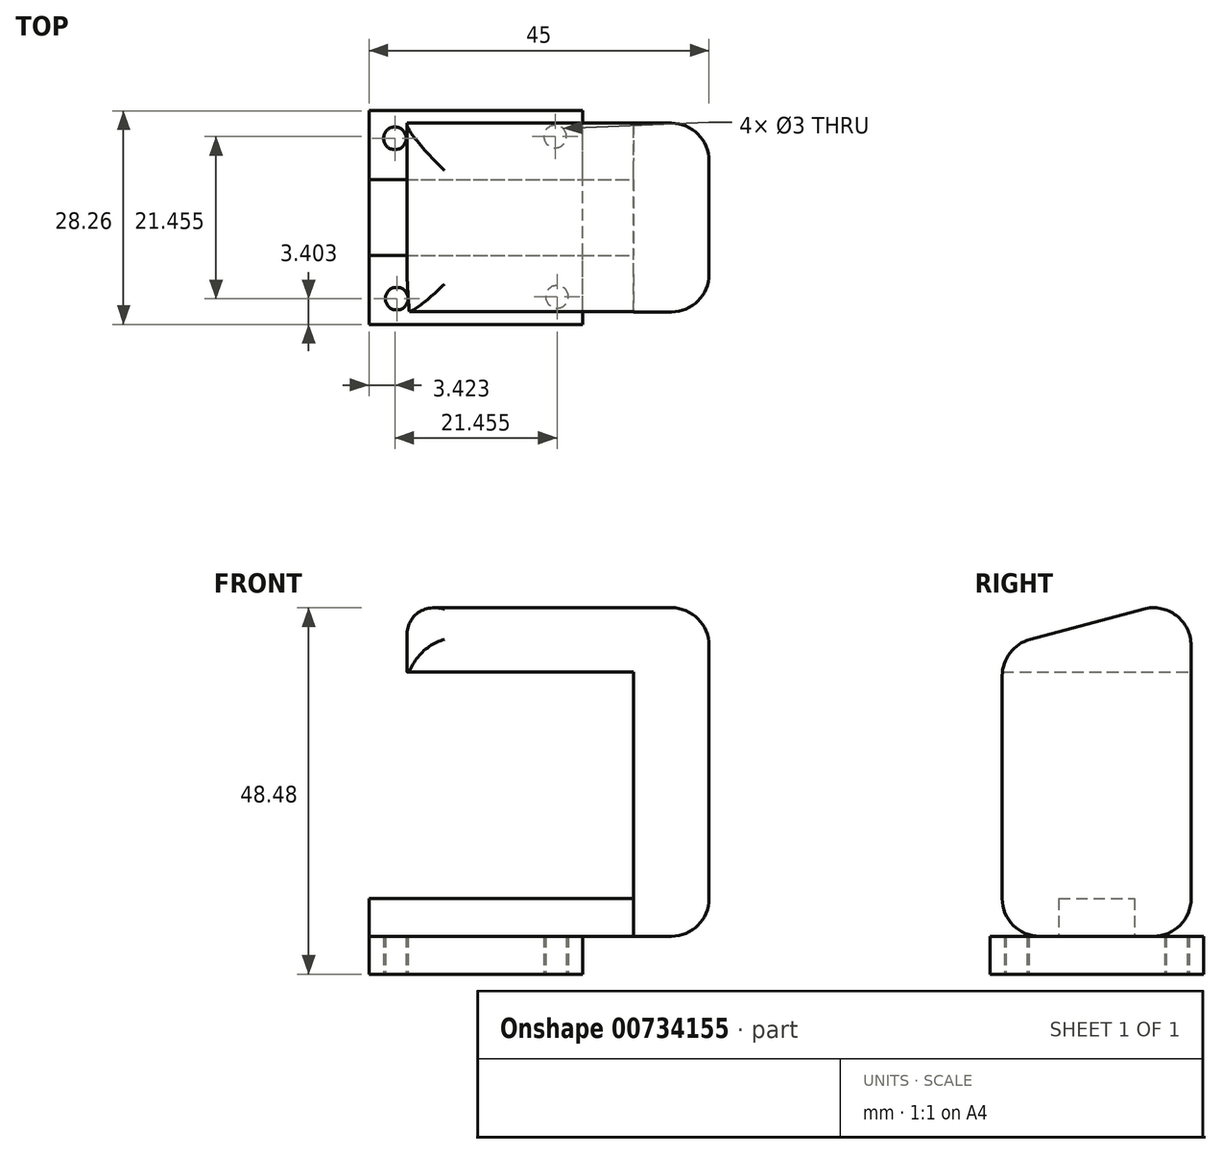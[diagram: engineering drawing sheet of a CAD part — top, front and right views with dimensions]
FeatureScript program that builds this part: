
annotation { "Feature Type Name" : "Feature", "Feature Type Description" : "" }
export const myFeature = defineFeature(function(context is Context, id is Id, definition is map)
    precondition{}
    {
        {
            var Q0;
            Q0=qCreatedBy(makeId("Top.planeOp"),FACE);
            var sketch = newSketch(context, id + "F0", { "sketchPlane" : qUnion([Q0])});
            skLineSegment(sketch, "E0.bottom", {"start": v(14.15, -14.13) * mm, "end": v(-14.15, -14.13) * mm});
            skLineSegment(sketch, "E0.top", {"start": v(14.15, 14.13) * mm, "end": v(-14.15, 14.13) * mm});
            skLineSegment(sketch, "E0.left", {"start": v(14.15, -14.13) * mm, "end": v(14.15, 14.13) * mm});
            skLineSegment(sketch, "E0.right", {"start": v(-14.15, -14.13) * mm, "end": v(-14.15, 14.13) * mm});
            skPoint(sketch, "E0.middle", {"position": v(0, 0) * mm});
            skCircle(sketch, "E1", {"center": v(-10.73, 10.48) * mm, "radius": 1.5 * mm});
            skCircle(sketch, "E2.1.0", {"center": v(-10.48, -10.73) * mm, "radius": 1.5 * mm});
            skCircle(sketch, "E2.2.0", {"center": v(10.73, -10.48) * mm, "radius": 1.5 * mm});
            skCircle(sketch, "E2.3.0", {"center": v(10.48, 10.73) * mm, "radius": 1.5 * mm});
            skSolve(sketch);
        }
        {
            var Q0;
            Q0 = qSketchRegion(id + "F0", true);
            extrude(context, id + "F1", {"entities" : qUnion([Q0]), "depth" : 5 * mm, "offsetDistance" : 25 * mm});
        }
        {
            var Q0;
            Q0=makeQuery(id+"F1.opExtrude","CAP_FACE",FACE,{"disambiguationData":[OSD([sQuery(id+"F0.wireOp",EDGE,"E0.bottom"),sQuery(id+"F0.wireOp",EDGE,"E0.top"),sQuery(id+"F0.wireOp",EDGE,"E0.left"),sQuery(id+"F0.wireOp",EDGE,"E0.right"),sQuery(id+"F0.wireOp",EDGE,"E1"),sQuery(id+"F0.wireOp",EDGE,"E2.1.0"),sQuery(id+"F0.wireOp",EDGE,"E2.2.0"),sQuery(id+"F0.wireOp",EDGE,"E2.3.0")])],"isStart":false});
            var sketch = newSketch(context, id + "F2", { "sketchPlane" : qUnion([Q0])});
            skLineSegment(sketch, "E3.bottom", {"start": v(-14.15, 5) * mm, "end": v(30.85, 5) * mm});
            skLineSegment(sketch, "E3.top", {"start": v(-14.15, -5) * mm, "end": v(30.85, -5) * mm});
            skLineSegment(sketch, "E3.left", {"start": v(-14.15, 5) * mm, "end": v(-14.15, -5) * mm});
            skLineSegment(sketch, "E3.right", {"start": v(30.85, 5) * mm, "end": v(30.85, -5) * mm});
            skPoint(sketch, "E4", {"position": v(14.15, 0) * mm});
            skPoint(sketch, "E5", {"position": v(-14.15, 0) * mm});
            skSolve(sketch);
        }
        {
            var Q0;
            Q0 = qSketchRegion(id + "F2", true);
            extrude(context, id + "F3", {"entities" : qUnion([Q0]), "operationType" : NewBodyOperationType.ADD, "depth" : 5 * mm, "offsetDistance" : 25 * mm});
        }
        {
            var Q0;
            Q0=makeQuery(id+"F3.opExtrude","CAP_FACE",FACE,{"disambiguationData":[OSD([sQuery(id+"F2.wireOp",EDGE,"E3.bottom"),sQuery(id+"F2.wireOp",EDGE,"E3.top"),sQuery(id+"F2.wireOp",EDGE,"E3.left"),sQuery(id+"F2.wireOp",EDGE,"E3.right")])],"isStart":true});
            var sketch = newSketch(context, id + "F4", { "sketchPlane" : qUnion([Q0])});
            skLineSegment(sketch, "E6.bottom", {"start": v(30.85, 12.5) * mm, "end": v(20.85, 12.5) * mm});
            skLineSegment(sketch, "E6.top", {"start": v(30.85, -12.5) * mm, "end": v(20.85, -12.5) * mm});
            skLineSegment(sketch, "E6.left", {"start": v(30.85, 12.5) * mm, "end": v(30.85, -12.5) * mm});
            skLineSegment(sketch, "E6.right", {"start": v(20.85, 12.5) * mm, "end": v(20.85, -12.5) * mm});
            skPoint(sketch, "E7", {"position": v(20.85, 0) * mm});
            skSolve(sketch);
        }
        {
            var Q0;
            Q0 = qSketchRegion(id + "F4", true);
            extrude(context, id + "F5", {"entities" : qUnion([Q0]), "operationType" : NewBodyOperationType.ADD, "oppositeDirection" : true, "depth" : 35 * mm, "offsetDistance" : 25 * mm});
        }
        {
            var Q0;
            Q0=makeQuery(id+"F5.opExtrude","SWEPT_FACE",FACE,{"disambiguationData":[OSD([sQuery(id+"F4.wireOp",EDGE,"E6.right")])]});
            var sketch = newSketch(context, id + "F6", { "sketchPlane" : qUnion([Q0])});
            skLineSegment(sketch, "E8", {"start": v(-12.5, 40) * mm, "end": v(-12.5, 50) * mm});
            skLineSegment(sketch, "E9", {"start": v(-12.5, 50) * mm, "end": v(12.5, 43.3) * mm});
            skLineSegment(sketch, "E10", {"start": v(12.5, 43.3) * mm, "end": v(12.5, 40) * mm});
            skLineSegment(sketch, "E11", {"start": v(12.5, 40) * mm, "end": v(-12.5, 40) * mm});
            skSolve(sketch);
        }
        {
            var Q0;
            Q0 = qSketchRegion(id + "F6", true);
            extrude(context, id + "F7", {"entities" : qUnion([Q0]), "operationType" : NewBodyOperationType.ADD, "depth" : 30 * mm, "offsetDistance" : 25 * mm, "hasSecondDirection" : true, "secondDirectionOppositeDirection" : true, "secondDirectionDepth" : 10 * mm});
        }
        {
            var Q0;
            Q0=makeQuery(id+"F7.opExtrude","SWEPT_EDGE",EDGE,{"disambiguationData":[OSD([sQuery(id+"F6.wireOp",EDGE,"E8"),sQuery(id+"F6.wireOp",EDGE,"E9")])]});
            var Q1;
            Q1=makeQuery(id+"F7.opExtrude","CAP_EDGE",EDGE,{"disambiguationData":[OSD([sQuery(id+"F6.wireOp",EDGE,"E9")])],"isStart":false});
            var Q2;
            Q2=makeQuery(id+"F7.opExtrude","SWEPT_EDGE",EDGE,{"disambiguationData":[OSD([sQuery(id+"F6.wireOp",EDGE,"E9"),sQuery(id+"F6.wireOp",EDGE,"E10")])]});
            var Q3;
            Q3=makeQuery(id+"F7.opExtrude","CAP_EDGE",EDGE,{"disambiguationData":[OSD([sQuery(id+"F6.wireOp",EDGE,"E9")])],"isStart":true});
            var Q4;
            Q4=makeQuery(id+"F7.boolean.opBoolean","MERGE",EDGE,{"derivedFrom":[makeQuery(id+"F5.opExtrude","SWEPT_EDGE",EDGE,{"disambiguationData":[OSD([sQuery(id+"F4.wireOp",EDGE,"E6.top"),sQuery(id+"F4.wireOp",EDGE,"E6.left")])]}),makeQuery(id+"F7.opExtrude","CAP_EDGE",EDGE,{"disambiguationData":[OSD([sQuery(id+"F6.wireOp",EDGE,"E8")])],"isStart":true})]});
            var Q5;
            Q5=makeQuery(id+"F7.boolean.opBoolean","MERGE",EDGE,{"derivedFrom":[makeQuery(id+"F5.opExtrude","SWEPT_EDGE",EDGE,{"disambiguationData":[OSD([sQuery(id+"F4.wireOp",EDGE,"E6.bottom"),sQuery(id+"F4.wireOp",EDGE,"E6.left")])]}),makeQuery(id+"F7.opExtrude","CAP_EDGE",EDGE,{"disambiguationData":[OSD([sQuery(id+"F6.wireOp",EDGE,"E10")])],"isStart":true})]});
            var Q6;
            Q6=makeQuery(id+"F5.boolean.opBoolean","MERGE",EDGE,{"derivedFrom":[makeQuery(id+"F3.opExtrude","CAP_EDGE",EDGE,{"disambiguationData":[OSD([sQuery(id+"F2.wireOp",EDGE,"E3.right")])],"isStart":true}),makeQuery(id+"F5.opExtrude","CAP_EDGE",EDGE,{"disambiguationData":[OSD([sQuery(id+"F4.wireOp",EDGE,"E6.left")])],"isStart":true})]});
            var Q7;
            Q7=makeQuery(id+"F5.opExtrude","CAP_EDGE",EDGE,{"disambiguationData":[OSD([sQuery(id+"F4.wireOp",EDGE,"E6.top")])],"isStart":true});
            var Q8;
            Q8=makeQuery(id+"F5.opExtrude","CAP_EDGE",EDGE,{"disambiguationData":[OSD([sQuery(id+"F4.wireOp",EDGE,"E6.bottom")])],"isStart":true});
            fillet(context, id + "F8", {"entities" : qUnion([Q0, Q1, Q2, Q3, Q4, Q5, Q6, Q7, Q8]), "radius" : 5 * mm, "tangentPropagation" : true, "allowEdgeOverflow" : false});
        }
    });
